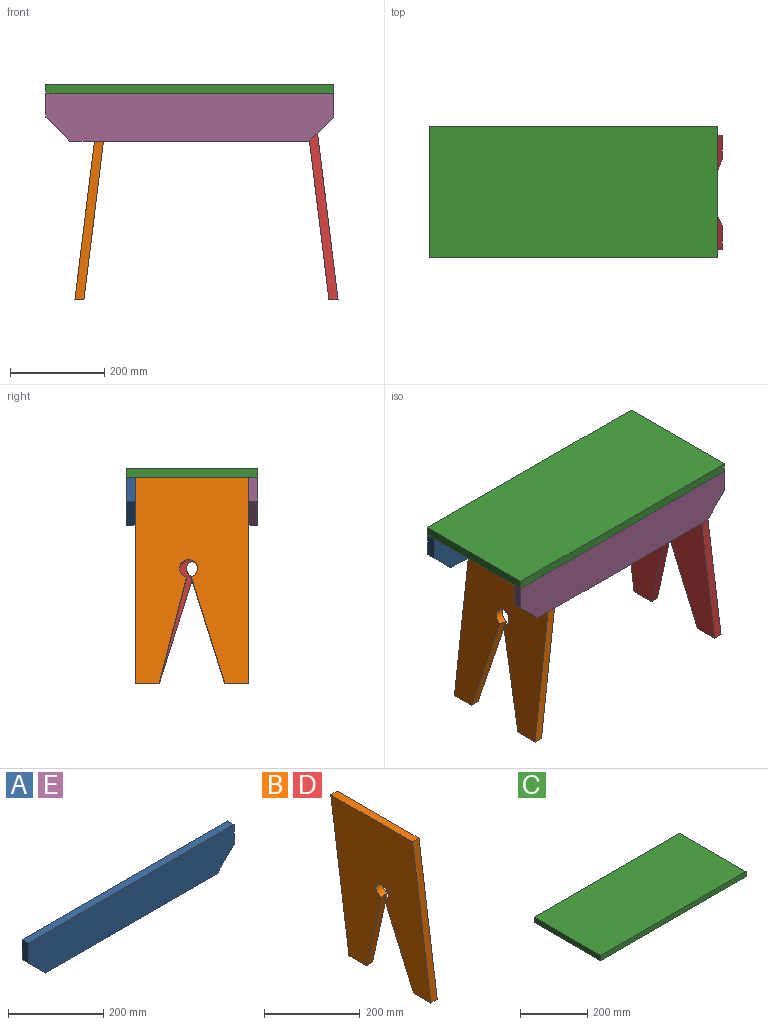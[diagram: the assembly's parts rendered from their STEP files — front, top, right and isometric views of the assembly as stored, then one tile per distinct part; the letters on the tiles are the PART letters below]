
ASSEMBLY  parts=5 mates=10
PART A: 8 faces, bbox 609.6x19.1x101.6 mm
  f0: plane 50.8x19.05mm, normal (1,0,0), area 967.7mm2, adj f1,f5,f6,f7
  f1: plane 609.6x19.05mm, normal (0,0,1), area 11612.9mm2, adj f0,f2,f6,f7
  f2: plane 50.8x19.05mm, normal (-1,0,0), area 967.7mm2, adj f1,f3,f6,f7
  f3: plane 50.8x50.8mm, normal (-0.71,0,-0.71), area 1368.6mm2, adj f2,f4,f6,f7
  f4: plane 508x19.05mm, normal (0,0,-1), area 9677.4mm2, adj f3,f5,f6,f7
  f5: plane 50.8x50.8mm, normal (0.71,0,-0.71), area 1368.6mm2, adj f0,f4,f6,f7
  f6: plane 609.6x101.6mm, normal (0,-1,0), area 59354.7mm2, adj f0,f1,f2,f3,f4,f5
  f7: plane 609.6x101.6mm, normal (0,1,0), area 59354.7mm2, adj f0,f1,f2,f3,f4,f5
PART B: 10 faces, bbox 73x241.3x438.2 mm
  f0: plane 51.53x19.19mm, normal (0,0,-1), area 982mm2, adj f2,f4,f6,f9
  f1: plane 241.3x19.19mm, normal (0,0,1), area 4631.3mm2, adj f2,f4,f5,f6
  f2: plane 438.15x241.3mm, normal (-0.99,0,-0.12), area 88583.8mm2, adj f0,f1,f3,f5,f6,f7,f8,f9
  f3: plane 51.4x19.19mm, normal (0,0,-1), area 980.7mm2, adj f2,f4,f5,f8
  f4: plane 438.15x241.3mm, normal (0.99,0,0.12), area 88258.6mm2, adj f0,f1,f3,f5,f6,f7,f8,f9
  f5: plane 438.15x72.99mm, normal (0,-1,0), area 8409.4mm2, adj f1,f2,f3,f4
  f6: plane 438.15x72.99mm, normal (0,1,0), area 8409.4mm2, adj f0,f1,f2,f4
  f7: cylinder r=19.05mm len=39.55mm, axis (0.99,0,0.12), area 2079.9mm2, adj f2,f4,f8,f9
  f8: plane 226.38x58.07mm, normal (0.03,0.97,-0.24), area 4460.6mm2, adj f2,f3,f4,f7
  f9: plane 226.66x71.26mm, normal (0.04,-0.95,-0.3), area 4533.8mm2, adj f0,f2,f4,f7
PART C: 6 faces, bbox 609.6x279.4x19.1 mm
  f0: plane 609.6x19.05mm, normal (0,1,0), area 11612.9mm2, adj f1,f3,f4,f5
  f1: plane 279.4x19.05mm, normal (-1,0,0), area 5322.6mm2, adj f0,f2,f4,f5
  f2: plane 609.6x19.05mm, normal (0,-1,0), area 11612.9mm2, adj f1,f3,f4,f5
  f3: plane 279.4x19.05mm, normal (1,0,0), area 5322.6mm2, adj f0,f2,f4,f5
  f4: plane 609.6x279.4mm, normal (0,0,1), area 170322.2mm2, adj f0,f1,f2,f3
  f5: plane 609.6x279.4mm, normal (0,0,-1), area 170322.2mm2, adj f0,f1,f2,f3
PART D: same geometry as B
PART E: same geometry as A
PLACE A t=(-71.91,45.63,-318.39)mm
PLACE B rot(axis=(0,0,1),180deg) t=(-242.41,-214.72,-444.71)mm
PLACE C t=(-71.91,-94.07,-267.59)mm fixed
PLACE D t=(169.05,26.58,-444.71)mm
PLACE E t=(-71.91,-214.72,-318.39)mm
MATE planar A.f7 <-> C.f0  axis (0,1,0) through (-71.91,45.63,-267.59)mm
MATE planar E.f1 <-> C.f5  axis (0,0,1) through (-71.91,-233.77,-267.59)mm
MATE planar E.f0 <-> C.f3  axis (1,0,0) through (232.89,-224.25,-292.99)mm
MATE planar A.f1 <-> C.f5  axis (0,0,1) through (232.89,45.63,-267.59)mm
MATE planar B.f1 <-> C.f5  axis (0,0,1) through (-252.01,-94.07,-267.59)mm
MATE planar E.f6 <-> C.f2  axis (0,-1,0) through (182.09,-233.77,-369.19)mm
MATE planar D.f1 <-> C.f5  axis (0,0,1) through (169.05,26.58,-267.59)mm
MATE planar A.f0 <-> C.f3  axis (1,0,0) through (232.89,36.1,-292.99)mm
MATE planar B.f6 <-> E.f7  axis (0,-1,0) through (-278.91,-214.72,-486.66)mm
MATE planar D.f6 <-> A.f6  axis (0,1,0) through (205.54,26.58,-486.66)mm
